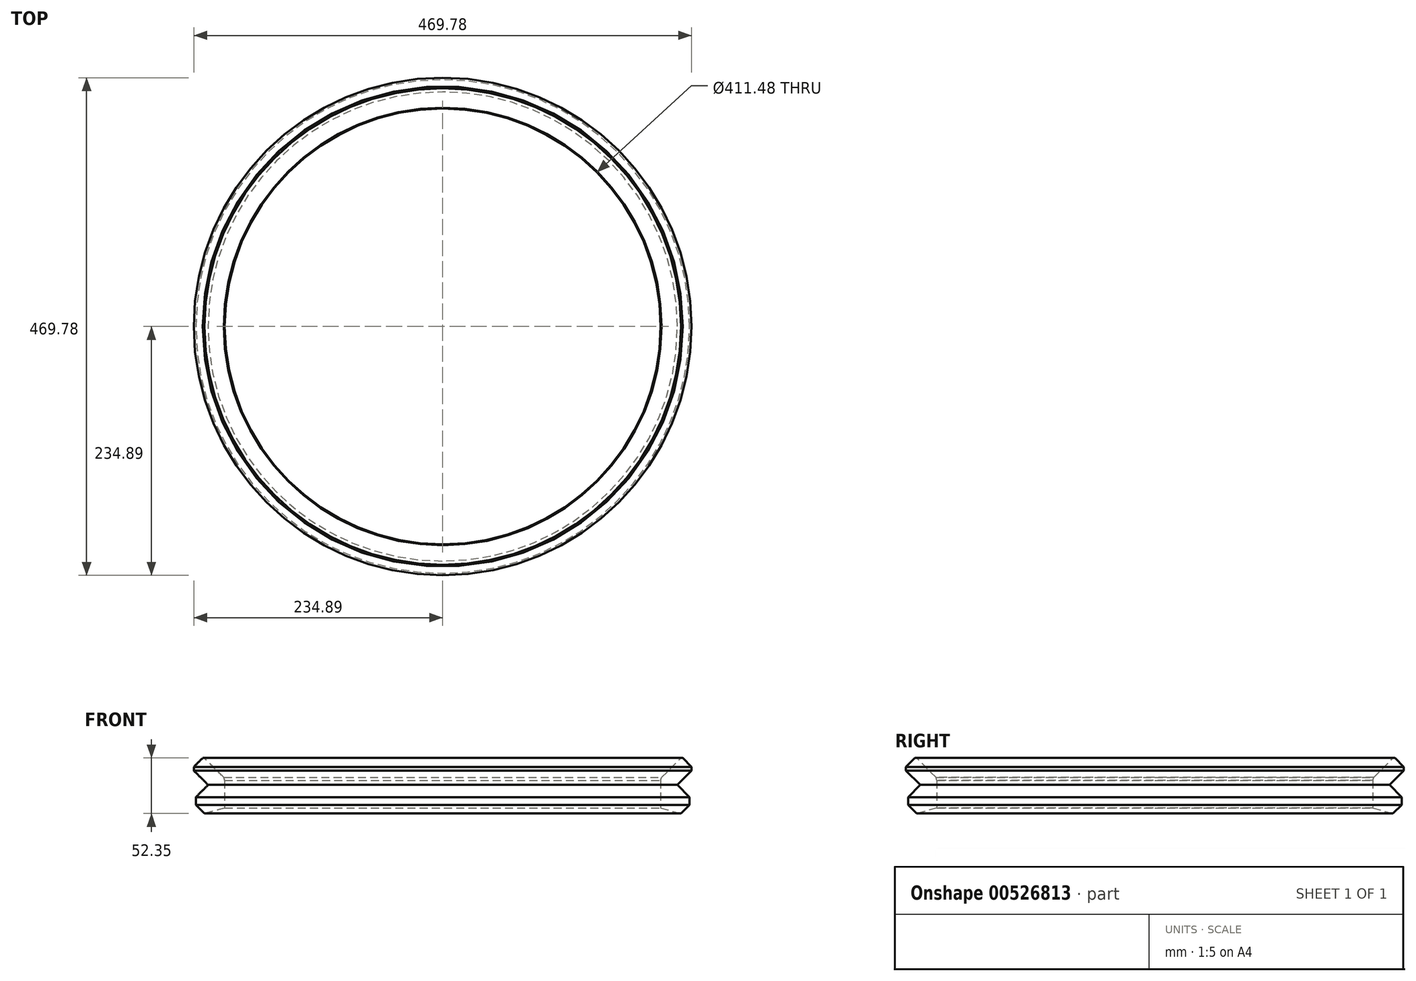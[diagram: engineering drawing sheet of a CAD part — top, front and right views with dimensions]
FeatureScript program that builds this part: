
annotation { "Feature Type Name" : "Feature", "Feature Type Description" : "" }
export const myFeature = defineFeature(function(context is Context, id is Id, definition is map)
    precondition{}
    {
        {
            var Q0;
            Q0=qCreatedBy(makeId("Front.planeOp"),FACE);
            var sketch = newSketch(context, id + "F0", { "sketchPlane" : qUnion([Q0])});
            skLineSegment(sketch, "E0.0", {"start": v(234.89, -8.32) * mm, "end": v(234.89, -11.88) * mm});
            skLineSegment(sketch, "E1.0", {"start": v(232.92, -36.88) * mm, "end": v(232.92, -44.27) * mm});
            skPoint(sketch, "E2", {"position": v(224.84, -52.35) * mm});
            skLineSegment(sketch, "E3", {"start": v(224.84, -52.35) * mm, "end": v(232.92, -44.27) * mm});
            skLineSegment(sketch, "E4", {"start": v(224.84, -52.35) * mm, "end": v(205.74, -47.23) * mm});
            skLineSegment(sketch, "E5", {"start": v(205.74, -21.18) * mm, "end": v(205.74, -47.23) * mm});
            skLineSegment(sketch, "E6", {"start": v(224.84, 0) * mm, "end": v(206.5, -18.34) * mm});
            skLineSegment(sketch, "E7", {"start": v(206.5, -18.34) * mm, "end": v(205.74, -21.18) * mm});
            skLineSegment(sketch, "E8", {"start": v(226.57, 0) * mm, "end": v(234.89, -8.32) * mm});
            skLineSegment(sketch, "E9.0", {"start": v(221.4, -25.36) * mm, "end": v(234.89, -11.88) * mm});
            skLineSegment(sketch, "E10.0", {"start": v(221.4, -25.36) * mm, "end": v(232.92, -36.88) * mm});
            skLineSegment(sketch, "E11", {"start": v(224.84, 0) * mm, "end": v(226.57, 0) * mm});
            skLineSegment(sketch, "E12", {"start": v(0, 0) * mm, "end": v(0, -109.84) * mm});
            skSolve(sketch);
        }
        {
            var Q0;
            Q0=sQuery(id+"F0.wireOp",EDGE,"E9.0");
            var Q1;
            Q1=sQuery(id+"F0.wireOp",EDGE,"E6");
            var Q2;
            Q2=sQuery(id+"F0.wireOp",EDGE,"E4");
            var Q3;
            Q3=sQuery(id+"F0.wireOp",EDGE,"E10.0");
            var Q4;
            Q4=sQuery(id+"F0.wireOp",EDGE,"E3");
            var Q5;
            Q5=sQuery(id+"F0.wireOp",EDGE,"E0.0");
            var Q6;
            Q6=sQuery(id+"F0.wireOp",EDGE,"E5");
            var Q7;
            Q7=sQuery(id+"F0.wireOp",EDGE,"E1.0");
            var Q8;
            Q8=sQuery(id+"F0.wireOp",EDGE,"E8");
            var Q9;
            Q9=sQuery(id+"F0.wireOp",EDGE,"E7");
            var Q10;
            Q10=sQuery(id+"F0.wireOp",EDGE,"E11");
            var Q11;
            Q11=sQuery(id+"F0.wireOp",EDGE,"E12");
            revolve(context, id + "F1", {"bodyType" : ToolBodyType.SURFACE, "surfaceEntities" : qUnion([Q0, Q1, Q2, Q3, Q4, Q5, Q6, Q7, Q8, Q9, Q10]), "axis" : qUnion([Q11]), "revolveType" : RevolveType.FULL});
        }
    });
